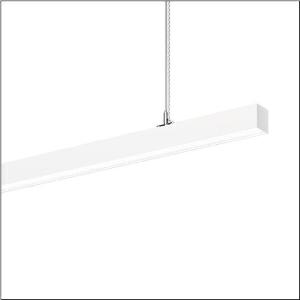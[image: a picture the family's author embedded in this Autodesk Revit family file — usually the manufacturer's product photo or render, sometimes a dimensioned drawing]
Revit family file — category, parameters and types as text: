
# Revit family: silica_r__21_51mx30tat4w_7b2a
name_source: partatom
category: Lighting Fixtures
units: mm (PartAtom-declared; Revit-internal decimal feet)

## family parameters
Cut with Voids When Loaded = No
Host = Face
Light Source = No
Part Type = Normal
Room Calculation Point = No
Round Connector Dimension = Use Diameter
Shared = No

## types (1)
- --- (1 x LED, 4120 lm, 33.8 W, 6500K)
    Apparent Load = 34 VA
    CIE Flux Codes = 47 79 96 58 100
    Color Rendering = 80
    Color Temperature = 6500K
    Default Elevation = 1800 mm
    Description = Silica® 21, office luminaire, primary optical cover: cover, of PMMA, opal, light emission: direct/indirect distribution, primary light characteristic: symmetric, installation type: suspended mounting, LED, rated luminous flux: 4.120lm, luminous efficacy: 116lm/W, light colour: 8tw, colour temperature: 2700..6500K, control gear: ECG DALI, with terminal, 3+2-pole, max. 2.5mm², mains connection: 220..240V, AC, 50/60Hz, rated input power: 35.5W, luminaire housing, of aluminium, traffic white (RAL 9016), length: 1.204mm, width: 53mm, height: 53mm, protection rating (complete): IP20, insulation class (complete): insulation class I (protective earthing), certification: CE, permissible operating ambient temperature: 0..+35°C, standard: EN 50419, packaging unit: 1 piece
    Height = 53 mm
    Lamp = 1 x LED
    Lamp Light Flux = 4120 lm
    Lamp Power = 33.8 W
    Lamp count = 1
    Length = 1204 mm
    Luminous efficacy = 122 lm/W
    Manufacturer = Siteco
    ModVariant = No
    Model = 51MX30TAT4W
    Mounting Place = Ceiling
    Mounting Type = Pendant
    Number of Poles = 1
    OnlyDefault = Yes
    Power Factor = 1
    Product Name = Silica® 21
    Product group = office luminaire | ceiling pendant
    ProductGroupID = 902
    Protection Class = Protection class I
    Protection Degree = IP 20
    RLX_Detail_Level = 1
    RLX_Emergency_Light_Flux = 0 lm
    RLX_Emergency_Type = 0
    RLX_Emergency_Type_DB = No
    RlxData = <blob elided: 18109 chars, md5=7b7371d8>
    Socket = socket
    Standby Power = 0 W
    System Light Flux = 4120 lm
    System Power = 34 W
    Type Comments = individual setting
    Type Image = l_1313629.jpg
    URL = http://relux.com
    VarID = @adj_089025
    Voltage = 0 V
    Weight = 0.00 kg
    Width = 53 mm

## geometry (parser evidence)
native form markers: Blend x4, Sweep x13
no freeform markers — native parametric forms only
